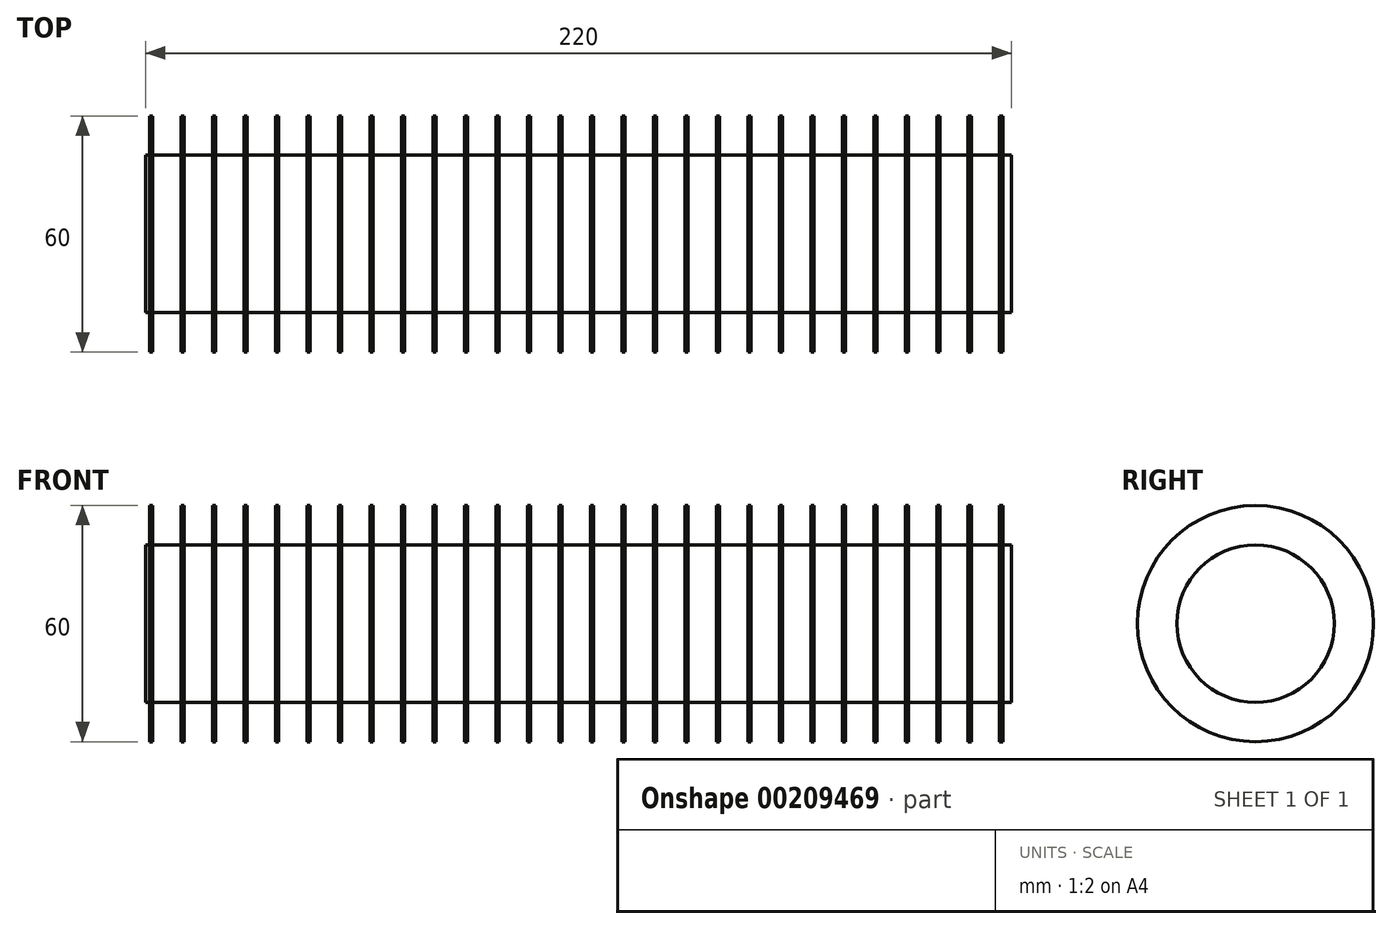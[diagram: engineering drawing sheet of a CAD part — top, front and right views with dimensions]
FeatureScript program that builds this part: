
annotation { "Feature Type Name" : "Feature", "Feature Type Description" : "" }
export const myFeature = defineFeature(function(context is Context, id is Id, definition is map)
    precondition{}
    {
        {
            var Q0;
            Q0=qCreatedBy(makeId("Right.planeOp"),FACE);
            var sketch = newSketch(context, id + "F0", { "sketchPlane" : qUnion([Q0])});
            skCircle(sketch, "E0", {"center": v(0, 0) * mm, "radius": 20 * mm});
            skSolve(sketch);
        }
        {
            var Q0;
            Q0=makeQuery(id+"F0.imprint","IMPRINT",FACE,{"disambiguationData":[TD([[makeQuery(id+"F0.imprint","IMPRINT",EDGE,{"derivedFrom":sQuery(id+"F0.wireOp",EDGE,"E0")}),1.0]])]});
            extrude(context, id + "F1", {"entities" : qUnion([Q0]), "depth" : 110 * mm, "hasSecondDirection" : true, "secondDirectionOppositeDirection" : true, "secondDirectionDepth" : 110 * mm});
        }
        {
            var Q0;
            Q0=qCreatedBy(makeId("Front.planeOp"),FACE);
            var sketch = newSketch(context, id + "F2", { "sketchPlane" : qUnion([Q0])});
            skLineSegment(sketch, "E1.bottom", {"start": v(-109, 30) * mm, "end": v(-108.2, 30) * mm});
            skLineSegment(sketch, "E1.top", {"start": v(-109, 17) * mm, "end": v(-108.2, 17) * mm});
            skLineSegment(sketch, "E1.left", {"start": v(-109, 30) * mm, "end": v(-109, 17) * mm});
            skLineSegment(sketch, "E1.right", {"start": v(-108.2, 30) * mm, "end": v(-108.2, 17) * mm});
            skLineSegment(sketch, "E2.1.0.0", {"start": v(-101, 17) * mm, "end": v(-100.2, 17) * mm});
            skLineSegment(sketch, "E2.1.0.1", {"start": v(-101, 30) * mm, "end": v(-101, 17) * mm});
            skLineSegment(sketch, "E2.1.0.2", {"start": v(-100.2, 30) * mm, "end": v(-100.2, 17) * mm});
            skLineSegment(sketch, "E2.1.0.3", {"start": v(-101, 30) * mm, "end": v(-100.2, 30) * mm});
            skLineSegment(sketch, "E2.2.0.0", {"start": v(-93, 17) * mm, "end": v(-92.2, 17) * mm});
            skLineSegment(sketch, "E2.2.0.1", {"start": v(-93, 30) * mm, "end": v(-93, 17) * mm});
            skLineSegment(sketch, "E2.2.0.2", {"start": v(-92.2, 30) * mm, "end": v(-92.2, 17) * mm});
            skLineSegment(sketch, "E2.2.0.3", {"start": v(-93, 30) * mm, "end": v(-92.2, 30) * mm});
            skLineSegment(sketch, "E2.3.0.0", {"start": v(-85, 17) * mm, "end": v(-84.2, 17) * mm});
            skLineSegment(sketch, "E2.3.0.1", {"start": v(-85, 30) * mm, "end": v(-85, 17) * mm});
            skLineSegment(sketch, "E2.3.0.2", {"start": v(-84.2, 30) * mm, "end": v(-84.2, 17) * mm});
            skLineSegment(sketch, "E2.3.0.3", {"start": v(-85, 30) * mm, "end": v(-84.2, 30) * mm});
            skLineSegment(sketch, "E2.4.0.0", {"start": v(-77, 17) * mm, "end": v(-76.2, 17) * mm});
            skLineSegment(sketch, "E2.4.0.1", {"start": v(-77, 30) * mm, "end": v(-77, 17) * mm});
            skLineSegment(sketch, "E2.4.0.2", {"start": v(-76.2, 30) * mm, "end": v(-76.2, 17) * mm});
            skLineSegment(sketch, "E2.4.0.3", {"start": v(-77, 30) * mm, "end": v(-76.2, 30) * mm});
            skLineSegment(sketch, "E2.5.0.0", {"start": v(-69, 17) * mm, "end": v(-68.2, 17) * mm});
            skLineSegment(sketch, "E2.5.0.1", {"start": v(-69, 30) * mm, "end": v(-69, 17) * mm});
            skLineSegment(sketch, "E2.5.0.2", {"start": v(-68.2, 30) * mm, "end": v(-68.2, 17) * mm});
            skLineSegment(sketch, "E2.5.0.3", {"start": v(-69, 30) * mm, "end": v(-68.2, 30) * mm});
            skLineSegment(sketch, "E2.6.0.0", {"start": v(-61, 17) * mm, "end": v(-60.2, 17) * mm});
            skLineSegment(sketch, "E2.6.0.1", {"start": v(-61, 30) * mm, "end": v(-61, 17) * mm});
            skLineSegment(sketch, "E2.6.0.2", {"start": v(-60.2, 30) * mm, "end": v(-60.2, 17) * mm});
            skLineSegment(sketch, "E2.6.0.3", {"start": v(-61, 30) * mm, "end": v(-60.2, 30) * mm});
            skLineSegment(sketch, "E2.7.0.0", {"start": v(-53, 17) * mm, "end": v(-52.2, 17) * mm});
            skLineSegment(sketch, "E2.7.0.1", {"start": v(-53, 30) * mm, "end": v(-53, 17) * mm});
            skLineSegment(sketch, "E2.7.0.2", {"start": v(-52.2, 30) * mm, "end": v(-52.2, 17) * mm});
            skLineSegment(sketch, "E2.7.0.3", {"start": v(-53, 30) * mm, "end": v(-52.2, 30) * mm});
            skLineSegment(sketch, "E2.8.0.0", {"start": v(-45, 17) * mm, "end": v(-44.2, 17) * mm});
            skLineSegment(sketch, "E2.8.0.1", {"start": v(-45, 30) * mm, "end": v(-45, 17) * mm});
            skLineSegment(sketch, "E2.8.0.2", {"start": v(-44.2, 30) * mm, "end": v(-44.2, 17) * mm});
            skLineSegment(sketch, "E2.8.0.3", {"start": v(-45, 30) * mm, "end": v(-44.2, 30) * mm});
            skLineSegment(sketch, "E2.9.0.0", {"start": v(-37, 17) * mm, "end": v(-36.2, 17) * mm});
            skLineSegment(sketch, "E2.9.0.1", {"start": v(-37, 30) * mm, "end": v(-37, 17) * mm});
            skLineSegment(sketch, "E2.9.0.2", {"start": v(-36.2, 30) * mm, "end": v(-36.2, 17) * mm});
            skLineSegment(sketch, "E2.9.0.3", {"start": v(-37, 30) * mm, "end": v(-36.2, 30) * mm});
            skLineSegment(sketch, "E2.10.0.0", {"start": v(-29, 17) * mm, "end": v(-28.2, 17) * mm});
            skLineSegment(sketch, "E2.10.0.1", {"start": v(-29, 30) * mm, "end": v(-29, 17) * mm});
            skLineSegment(sketch, "E2.10.0.2", {"start": v(-28.2, 30) * mm, "end": v(-28.2, 17) * mm});
            skLineSegment(sketch, "E2.10.0.3", {"start": v(-29, 30) * mm, "end": v(-28.2, 30) * mm});
            skLineSegment(sketch, "E2.11.0.0", {"start": v(-21, 17) * mm, "end": v(-20.2, 17) * mm});
            skLineSegment(sketch, "E2.11.0.1", {"start": v(-21, 30) * mm, "end": v(-21, 17) * mm});
            skLineSegment(sketch, "E2.11.0.2", {"start": v(-20.2, 30) * mm, "end": v(-20.2, 17) * mm});
            skLineSegment(sketch, "E2.11.0.3", {"start": v(-21, 30) * mm, "end": v(-20.2, 30) * mm});
            skLineSegment(sketch, "E2.12.0.0", {"start": v(-13, 17) * mm, "end": v(-12.2, 17) * mm});
            skLineSegment(sketch, "E2.12.0.1", {"start": v(-13, 30) * mm, "end": v(-13, 17) * mm});
            skLineSegment(sketch, "E2.12.0.2", {"start": v(-12.2, 30) * mm, "end": v(-12.2, 17) * mm});
            skLineSegment(sketch, "E2.12.0.3", {"start": v(-13, 30) * mm, "end": v(-12.2, 30) * mm});
            skLineSegment(sketch, "E2.13.0.0", {"start": v(-5, 17) * mm, "end": v(-4.2, 17) * mm});
            skLineSegment(sketch, "E2.13.0.1", {"start": v(-5, 30) * mm, "end": v(-5, 17) * mm});
            skLineSegment(sketch, "E2.13.0.2", {"start": v(-4.2, 30) * mm, "end": v(-4.2, 17) * mm});
            skLineSegment(sketch, "E2.13.0.3", {"start": v(-5, 30) * mm, "end": v(-4.2, 30) * mm});
            skLineSegment(sketch, "E2.14.0.0", {"start": v(3, 17) * mm, "end": v(3.8, 17) * mm});
            skLineSegment(sketch, "E2.14.0.1", {"start": v(3, 30) * mm, "end": v(3, 17) * mm});
            skLineSegment(sketch, "E2.14.0.2", {"start": v(3.8, 30) * mm, "end": v(3.8, 17) * mm});
            skLineSegment(sketch, "E2.14.0.3", {"start": v(3, 30) * mm, "end": v(3.8, 30) * mm});
            skLineSegment(sketch, "E2.15.0.0", {"start": v(11, 17) * mm, "end": v(11.8, 17) * mm});
            skLineSegment(sketch, "E2.15.0.1", {"start": v(11, 30) * mm, "end": v(11, 17) * mm});
            skLineSegment(sketch, "E2.15.0.2", {"start": v(11.8, 30) * mm, "end": v(11.8, 17) * mm});
            skLineSegment(sketch, "E2.15.0.3", {"start": v(11, 30) * mm, "end": v(11.8, 30) * mm});
            skLineSegment(sketch, "E2.direction1", {"start": v(-109, 17) * mm, "end": v(-101, 17) * mm, "construction": true});
            skLineSegment(sketch, "E3.0.16.0", {"start": v(19, 17) * mm, "end": v(19.8, 17) * mm});
            skLineSegment(sketch, "E3.3.16.0", {"start": v(19, 30) * mm, "end": v(19, 17) * mm});
            skLineSegment(sketch, "E3.6.16.0", {"start": v(19.8, 30) * mm, "end": v(19.8, 17) * mm});
            skLineSegment(sketch, "E3.9.16.0", {"start": v(19, 30) * mm, "end": v(19.8, 30) * mm});
            skLineSegment(sketch, "E3.0.17.0", {"start": v(27, 17) * mm, "end": v(27.8, 17) * mm});
            skLineSegment(sketch, "E3.3.17.0", {"start": v(27, 30) * mm, "end": v(27, 17) * mm});
            skLineSegment(sketch, "E3.6.17.0", {"start": v(27.8, 30) * mm, "end": v(27.8, 17) * mm});
            skLineSegment(sketch, "E3.9.17.0", {"start": v(27, 30) * mm, "end": v(27.8, 30) * mm});
            skLineSegment(sketch, "E3.0.18.0", {"start": v(35, 17) * mm, "end": v(35.8, 17) * mm});
            skLineSegment(sketch, "E3.3.18.0", {"start": v(35, 30) * mm, "end": v(35, 17) * mm});
            skLineSegment(sketch, "E3.6.18.0", {"start": v(35.8, 30) * mm, "end": v(35.8, 17) * mm});
            skLineSegment(sketch, "E3.9.18.0", {"start": v(35, 30) * mm, "end": v(35.8, 30) * mm});
            skLineSegment(sketch, "E3.0.19.0", {"start": v(43, 17) * mm, "end": v(43.8, 17) * mm});
            skLineSegment(sketch, "E3.3.19.0", {"start": v(43, 30) * mm, "end": v(43, 17) * mm});
            skLineSegment(sketch, "E3.6.19.0", {"start": v(43.8, 30) * mm, "end": v(43.8, 17) * mm});
            skLineSegment(sketch, "E3.9.19.0", {"start": v(43, 30) * mm, "end": v(43.8, 30) * mm});
            skLineSegment(sketch, "E3.0.20.0", {"start": v(51, 17) * mm, "end": v(51.8, 17) * mm});
            skLineSegment(sketch, "E3.3.20.0", {"start": v(51, 30) * mm, "end": v(51, 17) * mm});
            skLineSegment(sketch, "E3.6.20.0", {"start": v(51.8, 30) * mm, "end": v(51.8, 17) * mm});
            skLineSegment(sketch, "E3.9.20.0", {"start": v(51, 30) * mm, "end": v(51.8, 30) * mm});
            skLineSegment(sketch, "E3.0.21.0", {"start": v(59, 17) * mm, "end": v(59.8, 17) * mm});
            skLineSegment(sketch, "E3.3.21.0", {"start": v(59, 30) * mm, "end": v(59, 17) * mm});
            skLineSegment(sketch, "E3.6.21.0", {"start": v(59.8, 30) * mm, "end": v(59.8, 17) * mm});
            skLineSegment(sketch, "E3.9.21.0", {"start": v(59, 30) * mm, "end": v(59.8, 30) * mm});
            skLineSegment(sketch, "E3.0.22.0", {"start": v(67, 17) * mm, "end": v(67.8, 17) * mm});
            skLineSegment(sketch, "E3.3.22.0", {"start": v(67, 30) * mm, "end": v(67, 17) * mm});
            skLineSegment(sketch, "E3.6.22.0", {"start": v(67.8, 30) * mm, "end": v(67.8, 17) * mm});
            skLineSegment(sketch, "E3.9.22.0", {"start": v(67, 30) * mm, "end": v(67.8, 30) * mm});
            skLineSegment(sketch, "E3.0.23.0", {"start": v(75, 17) * mm, "end": v(75.8, 17) * mm});
            skLineSegment(sketch, "E3.3.23.0", {"start": v(75, 30) * mm, "end": v(75, 17) * mm});
            skLineSegment(sketch, "E3.6.23.0", {"start": v(75.8, 30) * mm, "end": v(75.8, 17) * mm});
            skLineSegment(sketch, "E3.9.23.0", {"start": v(75, 30) * mm, "end": v(75.8, 30) * mm});
            skLineSegment(sketch, "E3.0.24.0", {"start": v(83, 17) * mm, "end": v(83.8, 17) * mm});
            skLineSegment(sketch, "E3.3.24.0", {"start": v(83, 30) * mm, "end": v(83, 17) * mm});
            skLineSegment(sketch, "E3.6.24.0", {"start": v(83.8, 30) * mm, "end": v(83.8, 17) * mm});
            skLineSegment(sketch, "E3.9.24.0", {"start": v(83, 30) * mm, "end": v(83.8, 30) * mm});
            skLineSegment(sketch, "E3.0.25.0", {"start": v(91, 17) * mm, "end": v(91.8, 17) * mm});
            skLineSegment(sketch, "E3.3.25.0", {"start": v(91, 30) * mm, "end": v(91, 17) * mm});
            skLineSegment(sketch, "E3.6.25.0", {"start": v(91.8, 30) * mm, "end": v(91.8, 17) * mm});
            skLineSegment(sketch, "E3.9.25.0", {"start": v(91, 30) * mm, "end": v(91.8, 30) * mm});
            skLineSegment(sketch, "E3.0.26.0", {"start": v(99, 17) * mm, "end": v(99.8, 17) * mm});
            skLineSegment(sketch, "E3.3.26.0", {"start": v(99, 30) * mm, "end": v(99, 17) * mm});
            skLineSegment(sketch, "E3.6.26.0", {"start": v(99.8, 30) * mm, "end": v(99.8, 17) * mm});
            skLineSegment(sketch, "E3.9.26.0", {"start": v(99, 30) * mm, "end": v(99.8, 30) * mm});
            skLineSegment(sketch, "E4.0.27.0", {"start": v(107, 17) * mm, "end": v(107.8, 17) * mm});
            skLineSegment(sketch, "E4.3.27.0", {"start": v(107, 30) * mm, "end": v(107, 17) * mm});
            skLineSegment(sketch, "E4.6.27.0", {"start": v(107.8, 30) * mm, "end": v(107.8, 17) * mm});
            skLineSegment(sketch, "E4.9.27.0", {"start": v(107, 30) * mm, "end": v(107.8, 30) * mm});
            skSolve(sketch);
        }
        {
            var Q0;
            Q0 = qSketchRegion(id + "F2", true);
            var Q1;
            Q1=makeQuery(id+"F1.opExtrude","SWEPT_FACE",FACE,{"disambiguationData":[OSD([sQuery(id+"F0.wireOp",EDGE,"E0")])]});
            revolve(context, id + "F3", {"operationType" : NewBodyOperationType.ADD, "entities" : qUnion([Q0]), "axis" : qUnion([Q1]), "revolveType" : RevolveType.FULL});
        }
    });
